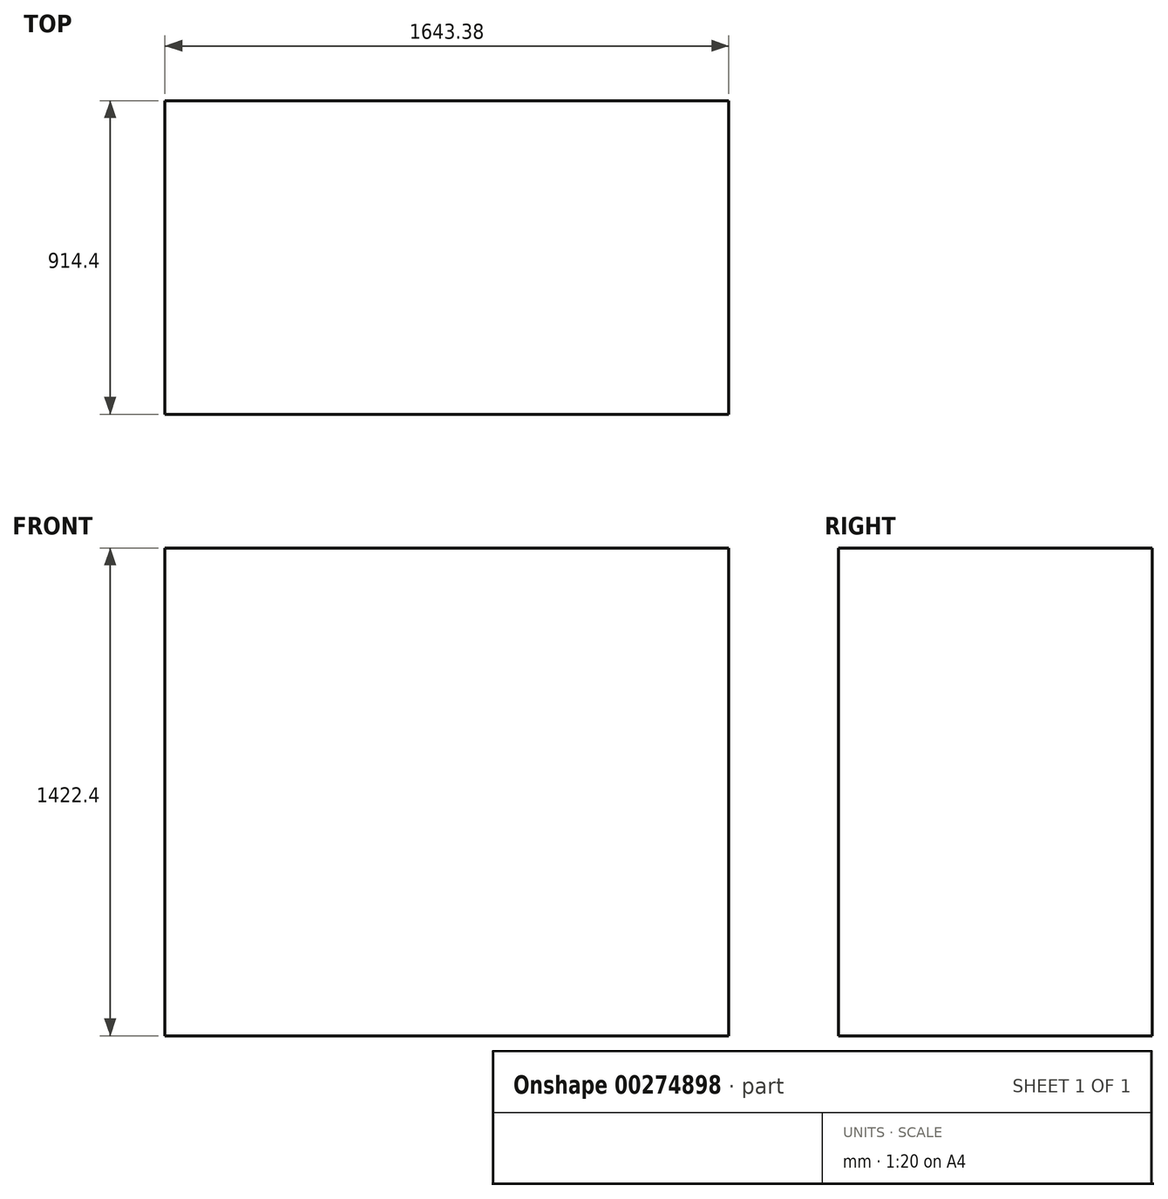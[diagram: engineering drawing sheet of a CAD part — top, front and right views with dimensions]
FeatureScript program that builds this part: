
annotation { "Feature Type Name" : "Feature", "Feature Type Description" : "" }
export const myFeature = defineFeature(function(context is Context, id is Id, definition is map)
    precondition{}
    {
        {
            var Q0;
            Q0=qCreatedBy(makeId("Top.planeOp"),FACE);
            var sketch = newSketch(context, id + "F0", { "sketchPlane" : qUnion([Q0])});
            skLineSegment(sketch, "E0.bottom", {"start": v(0, 0) * mm, "end": v(1066.8, 0) * mm});
            skLineSegment(sketch, "E0.top", {"start": v(0, 914.4) * mm, "end": v(1066.8, 914.4) * mm});
            skLineSegment(sketch, "E0.left", {"start": v(0, 0) * mm, "end": v(0, 914.4) * mm});
            skLineSegment(sketch, "E0.right", {"start": v(1066.8, 0) * mm, "end": v(1066.8, 914.4) * mm});
            skSolve(sketch);
        }
        {
            var Q0;
            Q0=makeQuery(id+"F0.imprint","IMPRINT",FACE,{"disambiguationData":[TD([[makeQuery(id+"F0.imprint","IMPRINT",EDGE,{"derivedFrom":sQuery(id+"F0.wireOp",EDGE,"E0.bottom")}),1.0]])]});
            extrude(context, id + "F1", {"entities" : qUnion([Q0]), "depth" : 1778 * mm});
        }
        {
            var Q0;
            Q0=makeQuery(id+"F1.opExtrude","SWEPT_FACE",FACE,{"disambiguationData":[OSD([sQuery(id+"F0.wireOp",EDGE,"E0.right")])]});
            extrude(context, id + "F2", {"entities" : qUnion([Q0]), "operationType" : NewBodyOperationType.ADD, "depth" : 576.58 * mm});
        }
        {
            var Q0;
            {var subQ0=sQuery(id+"F0.wireOp",EDGE,"E0.right");Q0=makeQuery(id+"F2.boolean.opBoolean","MERGE",FACE,{"derivedFrom":[makeQuery(id+"F1.opExtrude","CAP_FACE",FACE,{"disambiguationData":[OSD([sQuery(id+"F0.wireOp",EDGE,"E0.bottom"),sQuery(id+"F0.wireOp",EDGE,"E0.top"),sQuery(id+"F0.wireOp",EDGE,"E0.left"),subQ0])],"isStart":false}),makeQuery(id+"F2.opExtrude","SWEPT_FACE",FACE,{"disambiguationData":[OSD([subQ0]),TDD([makeQuery(id+"F1.opExtrude","CAP_EDGE",EDGE,{"disambiguationData":[OSD([subQ0])],"isStart":false})])]})]});}
            extrude(context, id + "F3", {"entities" : qUnion([Q0]), "operationType" : NewBodyOperationType.REMOVE, "oppositeDirection" : true, "depth" : 355.6 * mm});
        }
    });
